# Revit family: UNO-ME_G
name_source: partatom
category: Wyposażenie mechaniczne
revit_build: Autodesk Revit 2017 (Build: 20160225_1515(x64)
units: mm (PartAtom-declared; Revit-internal decimal feet)

## family parameters
Oparty na płaszczyźnie roboczej = Nie
Punkt obliczania pomieszczeń = Nie
Tnij formami wycięć po wczytaniu = Nie
Typ części = Normalny
Współdzielony = Nie
Wymiar okrągłego złącza = Użyj średnicy
Zawsze pionowo = Tak

## types (9) — shared parameters
Date = 09.2018
Frequency = 50 Hz
Producent = Rosenberg
Protection_class = IP54
URL = https://www.rosenberg.pl
Version = 1
max.Ambient_temperature = 120 °C

## per-type parameters (varying)
| type | A_ABH | A_ELS | A_WSD | Air_flow | B_ABH | B_ELS | B_GR | B_WSD | C_ELS | Current | Diameter | H_FUS | Height | L_FUS | Logo_scale | Model | Power | Pressure | Voltage | Weight[kg] | Width | a_connection | b_connection | stopnie |
| 50-355-G.4FA_230V | 300 mm  [stored 0.984252 ft] | 350 mm  [stored 1.14829 ft] | 600 mm  [stored 1.9685 ft] | 1920.0 m³/h | 240 mm  [stored 0.787402 ft] | 350 mm  [stored 1.14829 ft] | 464 mm  [stored 1.52231 ft] | 720 mm  [stored 2.3622 ft] | 20 mm  [stored 0.0656168 ft] | 2 A | 203 mm  [stored 0.66601 ft] | 32 mm  [stored 0.104987 ft] | 500 mm  [stored 1.64042 ft] | 600 mm  [stored 1.9685 ft] | 1 mm  [stored 0.00328084 ft] | 50-355-G.4FA | 0 kW | 308.0 Pa | 230 V | 44 | 540 mm  [stored 1.77165 ft] | 360 mm  [stored 1.1811 ft] | 180 mm  [stored 0.590551 ft] | 90.00° |
| 50-355-G.4FA_400V | 300 mm  [stored 0.984252 ft] | 350 mm  [stored 1.14829 ft] | 600 mm  [stored 1.9685 ft] | 1652.0 m³/h | 240 mm  [stored 0.787402 ft] | 350 mm  [stored 1.14829 ft] | 464 mm  [stored 1.52231 ft] | 720 mm  [stored 2.3622 ft] | 20 mm  [stored 0.0656168 ft] | 1 A | 228 mm  [stored 0.748031 ft] | 32 mm  [stored 0.104987 ft] | 500 mm  [stored 1.64042 ft] | 600 mm  [stored 1.9685 ft] | 1 mm  [stored 0.00328084 ft] | 50-355-G.4FA | 0 kW | 340.0 Pa | 400 V | 31 | 540 mm  [stored 1.77165 ft] | 360 mm  [stored 1.1811 ft] | 180 mm  [stored 0.590551 ft] | 150.00° |
| 67-400-G.5FF_230V | 380 mm | 450 mm  [stored 1.47638 ft] | 600 mm  [stored 1.9685 ft] | 2451.0 m³/h | 280 mm  [stored 0.918635 ft] | 450 mm  [stored 1.47638 ft] | 464 mm  [stored 1.52231 ft] | 720 mm  [stored 2.3622 ft] | 20 mm  [stored 0.0656168 ft] | 2 A | 250 mm  [stored 0.82021 ft] | 32 mm  [stored 0.104987 ft] | 670 mm  [stored 2.19816 ft] | 770 mm  [stored 2.52625 ft] | 1 mm  [stored 0.00328084 ft] | 67-400-G.5FF | 0 kW | 341.0 Pa | 230 V | 60 | 600 mm  [stored 1.9685 ft] | 530 mm  [stored 1.73885 ft] | 220 mm  [stored 0.721785 ft] | 150.00° |
| 67-400-G.5FF_400 | 380 mm | 450 mm  [stored 1.47638 ft] | 770 mm  [stored 2.52625 ft] | 2898.0 m³/h | 280 mm  [stored 0.918635 ft] | 450 mm  [stored 1.47638 ft] | 634 mm  [stored 2.08005 ft] | 800 mm  [stored 2.62467 ft] | 20 mm  [stored 0.0656168 ft] | 1 A | 250 mm  [stored 0.82021 ft] | 32 mm  [stored 0.104987 ft] | 670 mm  [stored 2.19816 ft] | 770 mm  [stored 2.52625 ft] | 1 mm  [stored 0.00328084 ft] | 67-400-G.5FF | 1 kW | 432.0 Pa | 400 V | 42.5 | 600 mm  [stored 1.9685 ft] | 530 mm  [stored 1.73885 ft] | 220 mm  [stored 0.721785 ft] | 150.00° |
| 67-450-G.6EF_230V | 380 mm | 450 mm  [stored 1.47638 ft] | 770 mm  [stored 2.52625 ft] | 3298.0 m³/h | 280 mm  [stored 0.918635 ft] | 450 mm  [stored 1.47638 ft] | 634 mm  [stored 2.08005 ft] | 800 mm  [stored 2.62467 ft] | 20 mm  [stored 0.0656168 ft] | 3 A | 300 mm  [stored 0.984252 ft] | 32 mm  [stored 0.104987 ft] | 670 mm  [stored 2.19816 ft] | 770 mm  [stored 2.52625 ft] | 1 mm  [stored 0.00328084 ft] | 67-450-G.6EF | 1 kW | 353.0 Pa | 230 V | 66 | 600 mm  [stored 1.9685 ft] | 530 mm  [stored 1.73885 ft] | 220 mm  [stored 0.721785 ft] | 150.00° |
| 80-500-G.6HA_400V | 430 mm | 580 mm  [stored 1.90289 ft] | 900 mm  [stored 2.95276 ft] | 5024.0 m³/h | 360 mm  [stored 1.1811 ft] | 580 mm  [stored 1.90289 ft] | 764 mm  [stored 2.50656 ft] | 890 mm  [stored 2.91995 ft] | 30 mm  [stored 0.0984252 ft] | 2 A | 325 mm  [stored 1.06627 ft] | 53 mm | 800 mm  [stored 2.62467 ft] | 900 mm  [stored 2.95276 ft] | 2 mm  [stored 0.00656168 ft] | 80-500-G.6HA | 1 kW | 605.0 Pa | 400 V | 96 | 740 mm  [stored 2.42782 ft] | 660 mm | 300 mm  [stored 0.984252 ft] | 150.00° |
| 67-450-G.6EF_400V | 380 mm | 450 mm  [stored 1.47638 ft] | 770 mm  [stored 2.52625 ft] | 3816.0 m³/h | 280 mm  [stored 0.918635 ft] | 450 mm  [stored 1.47638 ft] | 634 mm  [stored 2.08005 ft] | 800 mm  [stored 2.62467 ft] | 20 mm  [stored 0.0656168 ft] | 2 A | 300 mm  [stored 0.984252 ft] | 32 mm  [stored 0.104987 ft] | 670 mm  [stored 2.19816 ft] | 770 mm  [stored 2.52625 ft] | 1 mm  [stored 0.00328084 ft] | 67-450-G.6EF | 1 kW | 450.0 Pa | 400 V | 55 | 600 mm  [stored 1.9685 ft] | 530 mm  [stored 1.73885 ft] | 220 mm  [stored 0.721785 ft] | 150.00° |
| 80-560-G.6LA_400V | 430 mm | 580 mm  [stored 1.90289 ft] | 900 mm  [stored 2.95276 ft] | 5925.0 m³/h | 360 mm  [stored 1.1811 ft] | 580 mm  [stored 1.90289 ft] | 764 mm  [stored 2.50656 ft] | 890 mm  [stored 2.91995 ft] | 30 mm  [stored 0.0984252 ft] | 4 A | 360 mm  [stored 1.1811 ft] | 53 mm | 800 mm  [stored 2.62467 ft] | 900 mm  [stored 2.95276 ft] | 2 mm  [stored 0.00656168 ft] | 80-560-G.6LA | 2 kW | 724.0 Pa | 400 V | 102 | 740 mm  [stored 2.42782 ft] | 660 mm | 300 mm  [stored 0.984252 ft] | 150.00° |
| 80-630-G.8FF_400V | 430 mm | 580 mm  [stored 1.90289 ft] | 900 mm  [stored 2.95276 ft] | 7723.0 m³/h | 360 mm  [stored 1.1811 ft] | 580 mm  [stored 1.90289 ft] | 764 mm  [stored 2.50656 ft] | 1040 mm  [stored 3.41207 ft] | 30 mm  [stored 0.0984252 ft] | 6 A | 400 mm  [stored 1.31234 ft] | 53 mm | 800 mm  [stored 2.62467 ft] | 900 mm  [stored 2.95276 ft] | 2 mm  [stored 0.00656168 ft] | 80-630-G.8FF | 4 kW | 817.0 Pa | 400 V | 112 | 740 mm  [stored 2.42782 ft] | 660 mm | 300 mm  [stored 0.984252 ft] | 150.00° |

note: [stored X ft] marks values corroborated as IEEE doubles in the binary element streams (Revit-internal decimal feet)
